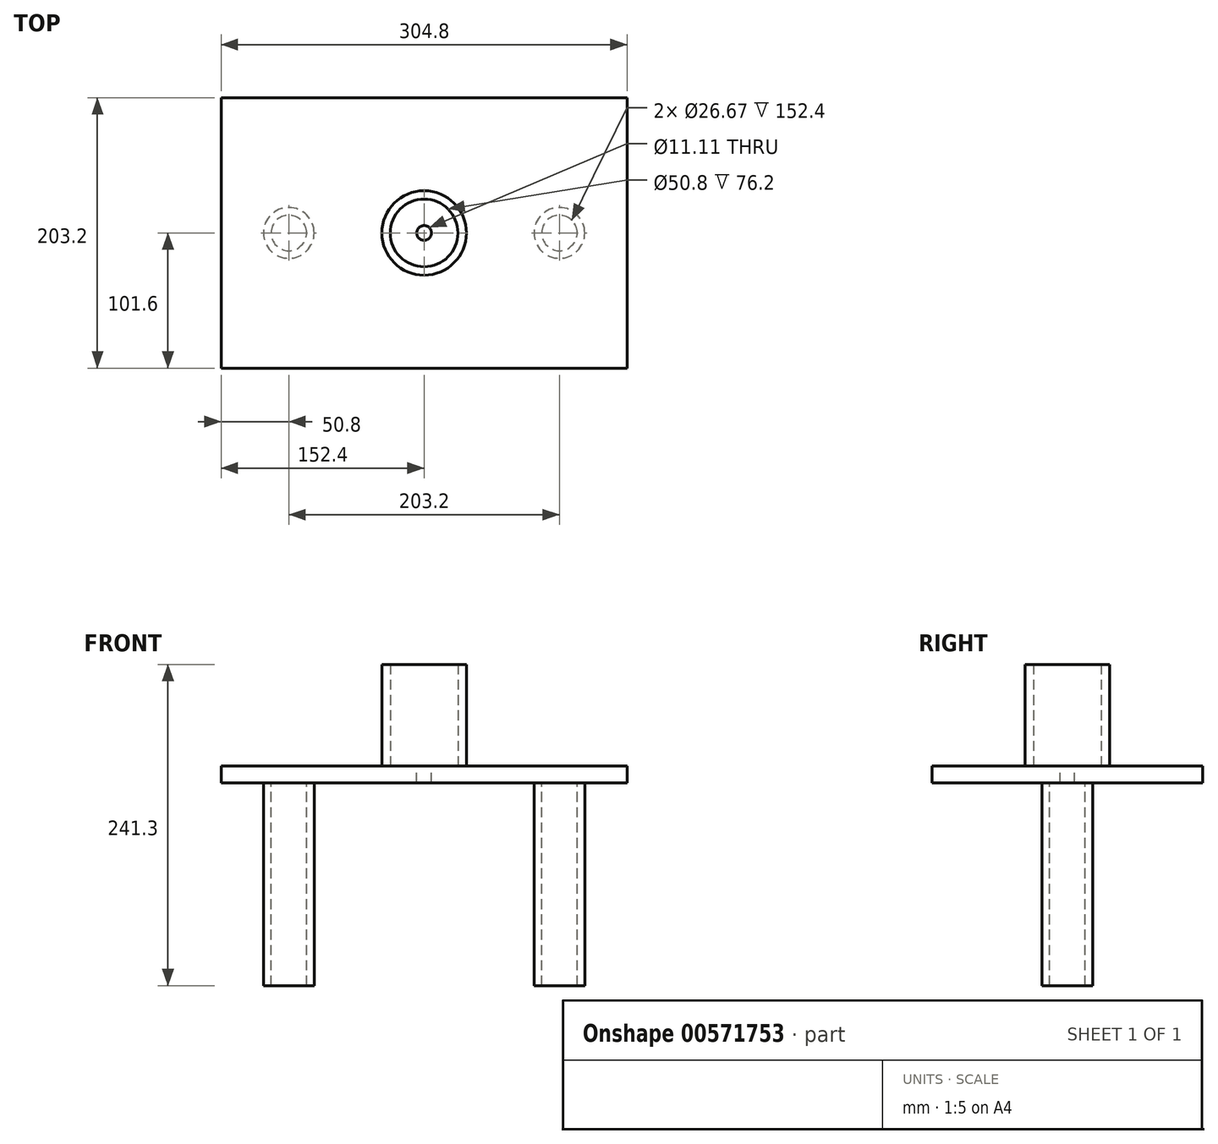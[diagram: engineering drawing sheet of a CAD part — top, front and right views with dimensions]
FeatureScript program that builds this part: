
annotation { "Feature Type Name" : "Feature", "Feature Type Description" : "" }
export const myFeature = defineFeature(function(context is Context, id is Id, definition is map)
    precondition{}
    {
        {
            var Q0;
            Q0=qCreatedBy(makeId("Front.planeOp"),FACE);
            var sketch = newSketch(context, id + "F0", { "sketchPlane" : qUnion([Q0])});
            skLineSegment(sketch, "E0.bottom", {"start": v(152.4, 6.35) * mm, "end": v(-152.4, 6.35) * mm});
            skLineSegment(sketch, "E0.top", {"start": v(152.4, -6.35) * mm, "end": v(-152.4, -6.35) * mm});
            skLineSegment(sketch, "E0.left", {"start": v(152.4, 6.35) * mm, "end": v(152.4, -6.35) * mm});
            skLineSegment(sketch, "E0.right", {"start": v(-152.4, 6.35) * mm, "end": v(-152.4, -6.35) * mm});
            skPoint(sketch, "E0.middle", {"position": v(0, 0) * mm});
            skSolve(sketch);
        }
        {
            var Q0;
            Q0 = qSketchRegion(id + "F0", true);
            extrude(context, id + "F1", {"entities" : qUnion([Q0]), "endBound" : BoundingType.SYMMETRIC, "depth" : 203.2 * mm, "offsetDistance" : 25.4 * mm});
        }
        {
            var Q0;
            Q0=makeQuery(id+"F1.opExtrude","SWEPT_FACE",FACE,{"disambiguationData":[OSD([sQuery(id+"F0.wireOp",EDGE,"E0.top")])]});
            var sketch = newSketch(context, id + "F2", { "sketchPlane" : qUnion([Q0])});
            skCircle(sketch, "E1", {"center": v(101.6, 0) * mm, "radius": 13.34 * mm});
            skCircle(sketch, "E2", {"center": v(101.6, 0) * mm, "radius": 19.05 * mm});
            skCircle(sketch, "E3.MirrorC", {"center": v(-101.6, 0) * mm, "radius": 19.05 * mm});
            skCircle(sketch, "E4.MirrorC", {"center": v(-101.6, 0) * mm, "radius": 13.34 * mm});
            skSolve(sketch);
        }
        {
            var Q0;
            Q0 = qSketchRegion(id + "F2", true);
            extrude(context, id + "F3", {"entities" : qUnion([Q0]), "operationType" : NewBodyOperationType.ADD, "depth" : 152.4 * mm, "offsetDistance" : 25.4 * mm});
        }
        {
            var Q0;
            Q0=makeQuery(id+"F1.opExtrude","SWEPT_FACE",FACE,{"disambiguationData":[OSD([sQuery(id+"F0.wireOp",EDGE,"E0.bottom")])]});
            var sketch = newSketch(context, id + "F4", { "sketchPlane" : qUnion([Q0])});
            skCircle(sketch, "E5", {"center": v(0, 0) * mm, "radius": 5.56 * mm});
            skSolve(sketch);
        }
        {
            var Q0;
            Q0 = qSketchRegion(id + "F4", true);
            extrude(context, id + "F5", {"entities" : qUnion([Q0]), "operationType" : NewBodyOperationType.REMOVE, "oppositeDirection" : true, "depth" : 25.4 * mm, "offsetDistance" : 25.4 * mm});
        }
        {
            var Q0;
            Q0=makeQuery(id+"F1.opExtrude","SWEPT_FACE",FACE,{"disambiguationData":[OSD([sQuery(id+"F0.wireOp",EDGE,"E0.bottom")])]});
            var sketch = newSketch(context, id + "F6", { "sketchPlane" : qUnion([Q0])});
            skCircle(sketch, "E6", {"center": v(0, 0) * mm, "radius": 25.4 * mm});
            skCircle(sketch, "E7", {"center": v(0, 0) * mm, "radius": 31.75 * mm});
            skSolve(sketch);
        }
        {
            var Q0;
            Q0 = qSketchRegion(id + "F6", true);
            extrude(context, id + "F7", {"entities" : qUnion([Q0]), "operationType" : NewBodyOperationType.ADD, "depth" : 76.2 * mm, "offsetDistance" : 25.4 * mm});
        }
    });
